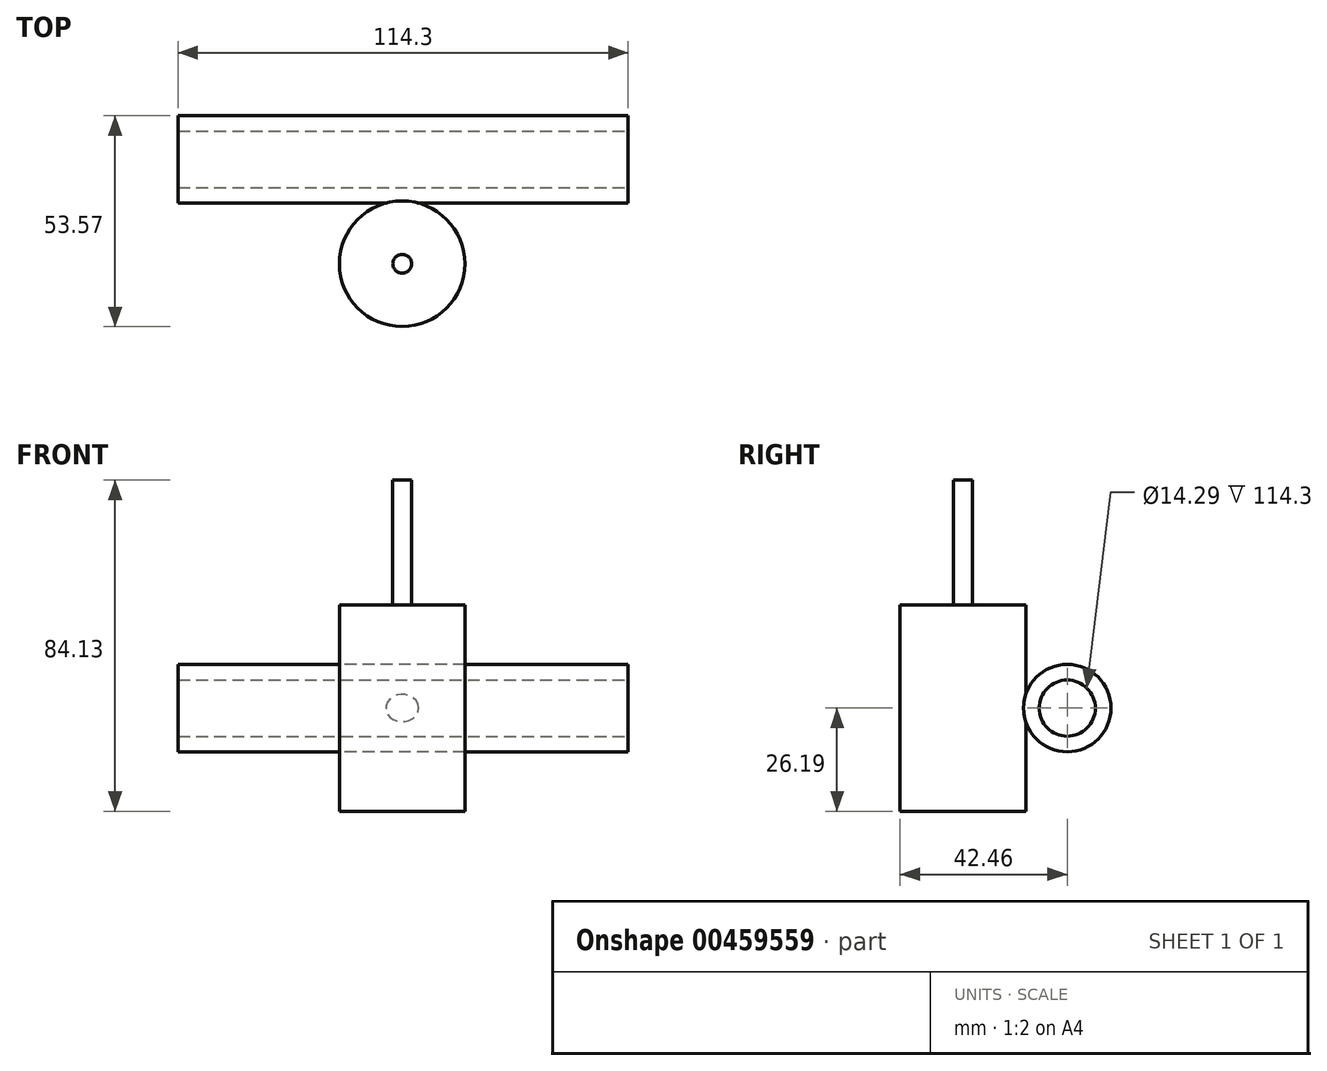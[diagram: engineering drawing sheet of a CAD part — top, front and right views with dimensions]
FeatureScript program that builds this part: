
annotation { "Feature Type Name" : "Feature", "Feature Type Description" : "" }
export const myFeature = defineFeature(function(context is Context, id is Id, definition is map)
    precondition{}
    {
        {
            var Q0;
            Q0=qCreatedBy(makeId("Right.planeOp"),FACE);
            var sketch = newSketch(context, id + "F0", { "sketchPlane" : qUnion([Q0])});
            skCircle(sketch, "E0", {"center": v(0, 0) * mm, "radius": 11.11 * mm});
            skSolve(sketch);
        }
        {
            var Q0;
            Q0=makeQuery(id+"F0.imprint","IMPRINT",FACE,{"disambiguationData":[TD([[makeQuery(id+"F0.imprint","IMPRINT",EDGE,{"derivedFrom":sQuery(id+"F0.wireOp",EDGE,"E0")}),1.0]])]});
            extrude(context, id + "F1", {"entities" : qUnion([Q0]), "endBound" : BoundingType.SYMMETRIC, "depth" : 114.3 * mm});
        }
        {
            var Q0;
            Q0=makeQuery(id+"F1.opExtrude","CAP_FACE",FACE,{"disambiguationData":[OSD([sQuery(id+"F0.wireOp",EDGE,"E0")])],"isStart":false});
            var sketch = newSketch(context, id + "F2", { "sketchPlane" : qUnion([Q0])});
            skSolve(sketch);
        }
        {
            var Q0;
            Q0=makeQuery(id+"F2.imprint","IMPRINT",FACE,{"disambiguationData":[TD([[makeQuery(id+"F2.imprint","IMPRINT",EDGE,{"derivedFrom":makeQuery(id+"F1.opExtrude","CAP_EDGE",EDGE,{"disambiguationData":[OSD([sQuery(id+"F0.wireOp",EDGE,"E0")])],"isStart":false})}),1.0]])]});
            var sketch = newSketch(context, id + "F3", { "sketchPlane" : qUnion([Q0])});
            skCircle(sketch, "E1", {"center": v(0, 0) * mm, "radius": 7.14 * mm});
            skSolve(sketch);
        }
        {
            var Q0;
            Q0=qSketchRegion(id+"F3",true);
            extrude(context, id + "F4", {"entities" : qUnion([Q0]), "operationType" : NewBodyOperationType.REMOVE, "oppositeDirection" : true, "depth" : 114.3 * mm});
        }
        {
            var Q0;
            Q0=qCreatedBy(makeId("Top.planeOp"),FACE);
            var sketch = newSketch(context, id + "F5", { "sketchPlane" : qUnion([Q0])});
            skCircle(sketch, "E2", {"center": v(-0.23, -26.5) * mm, "radius": 15.95 * mm});
            skSolve(sketch);
        }
        {
            var Q0;
            Q0=qSketchRegion(id+"F5",true);
            extrude(context, id + "F6", {"entities" : qUnion([Q0]), "operationType" : NewBodyOperationType.ADD, "endBound" : BoundingType.SYMMETRIC, "depth" : 52.4 * mm});
        }
        {
            var Q0;
            Q0=makeQuery(id+"F6.opExtrude","CAP_FACE",FACE,{"disambiguationData":[OSD([sQuery(id+"F5.wireOp",EDGE,"E2")])],"isStart":false});
            var sketch = newSketch(context, id + "F7", { "sketchPlane" : qUnion([Q0])});
            skCircle(sketch, "E3", {"center": v(-0.23, -26.5) * mm, "radius": 2.38 * mm});
            skSolve(sketch);
        }
        {
            var Q0;
            Q0=qSketchRegion(id+"F7",true);
            extrude(context, id + "F8", {"entities" : qUnion([Q0]), "operationType" : NewBodyOperationType.ADD, "depth" : 31.75 * mm});
        }
    });
